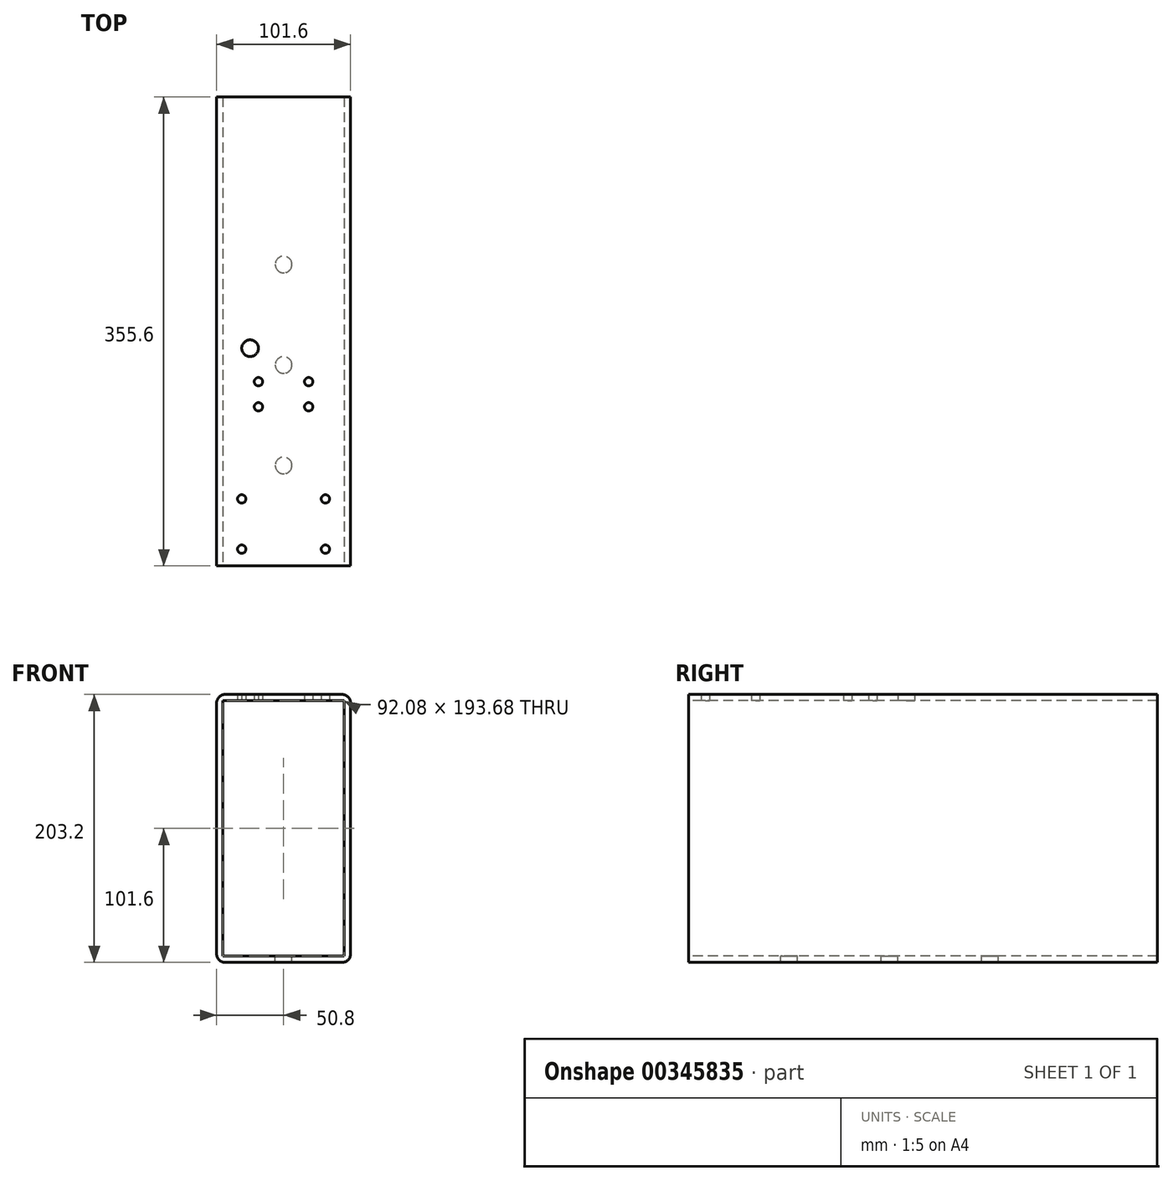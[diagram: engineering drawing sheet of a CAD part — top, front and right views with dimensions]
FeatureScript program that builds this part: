
annotation { "Feature Type Name" : "Feature", "Feature Type Description" : "" }
export const myFeature = defineFeature(function(context is Context, id is Id, definition is map)
    precondition{}
    {
        {
            var Q0;
            Q0=qCreatedBy(makeId("Front.planeOp"),FACE);
            var sketch = newSketch(context, id + "F3", { "sketchPlane" : qUnion([Q0])});
            skLineSegment(sketch, "E0.bottom", {"start": v(-44.45, -101.6) * mm, "end": v(44.45, -101.6) * mm});
            skLineSegment(sketch, "E0.top", {"start": v(-44.45, 101.6) * mm, "end": v(44.45, 101.6) * mm});
            skLineSegment(sketch, "E0.left", {"start": v(-50.8, -95.25) * mm, "end": v(-50.8, 95.25) * mm});
            skLineSegment(sketch, "E0.right", {"start": v(50.8, -95.25) * mm, "end": v(50.8, 95.25) * mm});
            skPoint(sketch, "E0.middle", {"position": v(0, 0) * mm});
            skLineSegment(sketch, "E1.bottom", {"start": v(46.04, -96.84) * mm, "end": v(-46.04, -96.84) * mm});
            skLineSegment(sketch, "E1.top", {"start": v(46.04, 96.84) * mm, "end": v(-46.04, 96.84) * mm});
            skLineSegment(sketch, "E1.left", {"start": v(46.04, -96.84) * mm, "end": v(46.04, 96.84) * mm});
            skLineSegment(sketch, "E1.right", {"start": v(-46.04, -96.84) * mm, "end": v(-46.04, 96.84) * mm});
            skPoint(sketch, "E2.visualSharp", {"position": v(-50.8, 101.6) * mm});
            skArc(sketch, "E2.filletArc", {"start": v(-44.45, 101.6) * mm, "mid": v(-48.94, 99.74) * mm, "end": v(-50.8, 95.25) * mm});
            skPoint(sketch, "E3.visualSharp", {"position": v(-50.8, -101.6) * mm});
            skArc(sketch, "E3.filletArc", {"start": v(-50.8, -95.25) * mm, "mid": v(-48.94, -99.74) * mm, "end": v(-44.45, -101.6) * mm});
            skPoint(sketch, "E4.visualSharp", {"position": v(50.8, -101.6) * mm});
            skArc(sketch, "E4.filletArc", {"start": v(44.45, -101.6) * mm, "mid": v(48.94, -99.74) * mm, "end": v(50.8, -95.25) * mm});
            skPoint(sketch, "E5.visualSharp", {"position": v(50.8, 101.6) * mm});
            skArc(sketch, "E5.filletArc", {"start": v(50.8, 95.25) * mm, "mid": v(48.94, 99.74) * mm, "end": v(44.45, 101.6) * mm});
            skSolve(sketch);
        }
        {
            var Q0;
            Q0=makeQuery(id+"F3.imprint","IMPRINT",FACE,{"disambiguationData":[TD([[makeQuery(id+"F3.imprint","IMPRINT",EDGE,{"derivedFrom":sQuery(id+"F3.wireOp",EDGE,"E0.bottom")}),1.0]])]});
            extrude(context, id + "F4", {"entities" : qUnion([Q0]), "oppositeDirection" : true, "depth" : 355.6 * mm});
        }
        {
            var Q0;
            Q0=qCreatedBy(makeId("Top.planeOp"),FACE);
            var sketch = newSketch(context, id + "F5", { "sketchPlane" : qUnion([Q0])});
            skPoint(sketch, "E6", {"position": v(0, 76.2) * mm});
            skPoint(sketch, "E7", {"position": v(0, 152.4) * mm});
            skPoint(sketch, "E8", {"position": v(0, 228.6) * mm});
            skSolve(sketch);
        }
        {
            var Q0;
            Q0=sQuery(id+"F5.wireOp",VERTEX,"E8");
            var Q1;
            Q1=sQuery(id+"F5.wireOp",VERTEX,"E7");
            var Q2;
            Q2=sQuery(id+"F5.wireOp",VERTEX,"E6");
            var Q3;
            Q3=makeQuery(id+"F4.opExtrude","SWEPT_BODY",BODY,{"disambiguationData":[OSD([sQuery(id+"F3.wireOp",EDGE,"E0.bottom"),sQuery(id+"F3.wireOp",EDGE,"E0.top"),sQuery(id+"F3.wireOp",EDGE,"E0.left"),sQuery(id+"F3.wireOp",EDGE,"E0.right"),sQuery(id+"F3.wireOp",EDGE,"E1.bottom"),sQuery(id+"F3.wireOp",EDGE,"E1.top"),sQuery(id+"F3.wireOp",EDGE,"E1.left"),sQuery(id+"F3.wireOp",EDGE,"E1.right"),sQuery(id+"F3.wireOp",EDGE,"E2.filletArc"),sQuery(id+"F3.wireOp",EDGE,"E3.filletArc"),sQuery(id+"F3.wireOp",EDGE,"E4.filletArc"),sQuery(id+"F3.wireOp",EDGE,"E5.filletArc")])]});
            hole(context, id + "F0", {"style" : HoleStyle.SIMPLE, "endStyle" : HoleEndStyle.THROUGH, "holeDiameter" : 12.7 * mm, "locations" : qUnion([Q0, Q1, Q2]), "scope" : qUnion([Q3]), "isTappedThrough" : true});
        }
        {
            var Q0;
            Q0=qCreatedBy(makeId("Top.planeOp"),FACE);
            var sketch = newSketch(context, id + "F1", { "sketchPlane" : qUnion([Q0])});
            skPoint(sketch, "E9", {"position": v(0, 165.1) * mm});
            skPoint(sketch, "E10", {"position": v(-25.4, 165.1) * mm});
            skPoint(sketch, "E11", {"position": v(0, 12.7) * mm});
            skPoint(sketch, "E12", {"position": v(-31.75, 12.7) * mm});
            skPoint(sketch, "E13", {"position": v(31.75, 12.7) * mm});
            skPoint(sketch, "E14", {"position": v(-31.75, 50.8) * mm});
            skPoint(sketch, "E15", {"position": v(31.75, 50.8) * mm});
            skPoint(sketch, "E16", {"position": v(-31.75, 139.7) * mm});
            skPoint(sketch, "E17", {"position": v(31.75, 139.7) * mm});
            skPoint(sketch, "E18", {"position": v(-19.05, 139.7) * mm});
            skPoint(sketch, "E19", {"position": v(19.05, 139.7) * mm});
            skPoint(sketch, "E20", {"position": v(19.05, 120.65) * mm});
            skPoint(sketch, "E21", {"position": v(-19.05, 120.65) * mm});
            skSolve(sketch);
        }
        {
            var Q0;
            Q0=sQuery(id+"F1.wireOp",VERTEX,"E10");
            var Q1;
            Q1=makeQuery(id+"F4.opExtrude","SWEPT_BODY",BODY,{"disambiguationData":[OSD([sQuery(id+"F3.wireOp",EDGE,"E0.bottom"),sQuery(id+"F3.wireOp",EDGE,"E0.top"),sQuery(id+"F3.wireOp",EDGE,"E0.left"),sQuery(id+"F3.wireOp",EDGE,"E0.right"),sQuery(id+"F3.wireOp",EDGE,"E1.bottom"),sQuery(id+"F3.wireOp",EDGE,"E1.top"),sQuery(id+"F3.wireOp",EDGE,"E1.left"),sQuery(id+"F3.wireOp",EDGE,"E1.right"),sQuery(id+"F3.wireOp",EDGE,"E2.filletArc"),sQuery(id+"F3.wireOp",EDGE,"E3.filletArc"),sQuery(id+"F3.wireOp",EDGE,"E4.filletArc"),sQuery(id+"F3.wireOp",EDGE,"E5.filletArc")])]});
            hole(context, id + "F2", {"style" : HoleStyle.SIMPLE, "endStyle" : HoleEndStyle.THROUGH, "oppositeDirection" : true, "holeDiameter" : 12.7 * mm, "locations" : qUnion([Q0]), "scope" : qUnion([Q1]), "isTappedThrough" : true});
        }
        {
            var Q0;
            Q0=sQuery(id+"F1.wireOp",VERTEX,"E13");
            var Q1;
            Q1=sQuery(id+"F1.wireOp",VERTEX,"E12");
            var Q2;
            Q2=sQuery(id+"F1.wireOp",VERTEX,"E14");
            var Q3;
            Q3=sQuery(id+"F1.wireOp",VERTEX,"E15");
            var Q4;
            Q4=sQuery(id+"F1.wireOp",VERTEX,"E19");
            var Q5;
            Q5=sQuery(id+"F1.wireOp",VERTEX,"E18");
            var Q6;
            Q6=sQuery(id+"F1.wireOp",VERTEX,"E20");
            var Q7;
            Q7=sQuery(id+"F1.wireOp",VERTEX,"E21");
            var Q8;
            Q8=makeQuery(id+"F4.opExtrude","SWEPT_BODY",BODY,{"disambiguationData":[OSD([sQuery(id+"F3.wireOp",EDGE,"E0.bottom"),sQuery(id+"F3.wireOp",EDGE,"E0.top"),sQuery(id+"F3.wireOp",EDGE,"E0.left"),sQuery(id+"F3.wireOp",EDGE,"E0.right"),sQuery(id+"F3.wireOp",EDGE,"E1.bottom"),sQuery(id+"F3.wireOp",EDGE,"E1.top"),sQuery(id+"F3.wireOp",EDGE,"E1.left"),sQuery(id+"F3.wireOp",EDGE,"E1.right"),sQuery(id+"F3.wireOp",EDGE,"E2.filletArc"),sQuery(id+"F3.wireOp",EDGE,"E3.filletArc"),sQuery(id+"F3.wireOp",EDGE,"E4.filletArc"),sQuery(id+"F3.wireOp",EDGE,"E5.filletArc")])]});
            hole(context, id + "F6", {"style" : HoleStyle.SIMPLE, "endStyle" : HoleEndStyle.THROUGH, "oppositeDirection" : true, "holeDiameter" : 6.35 * mm, "locations" : qUnion([Q0, Q1, Q2, Q3, Q4, Q5, Q6, Q7]), "scope" : qUnion([Q8]), "isTappedThrough" : true});
        }
    });
